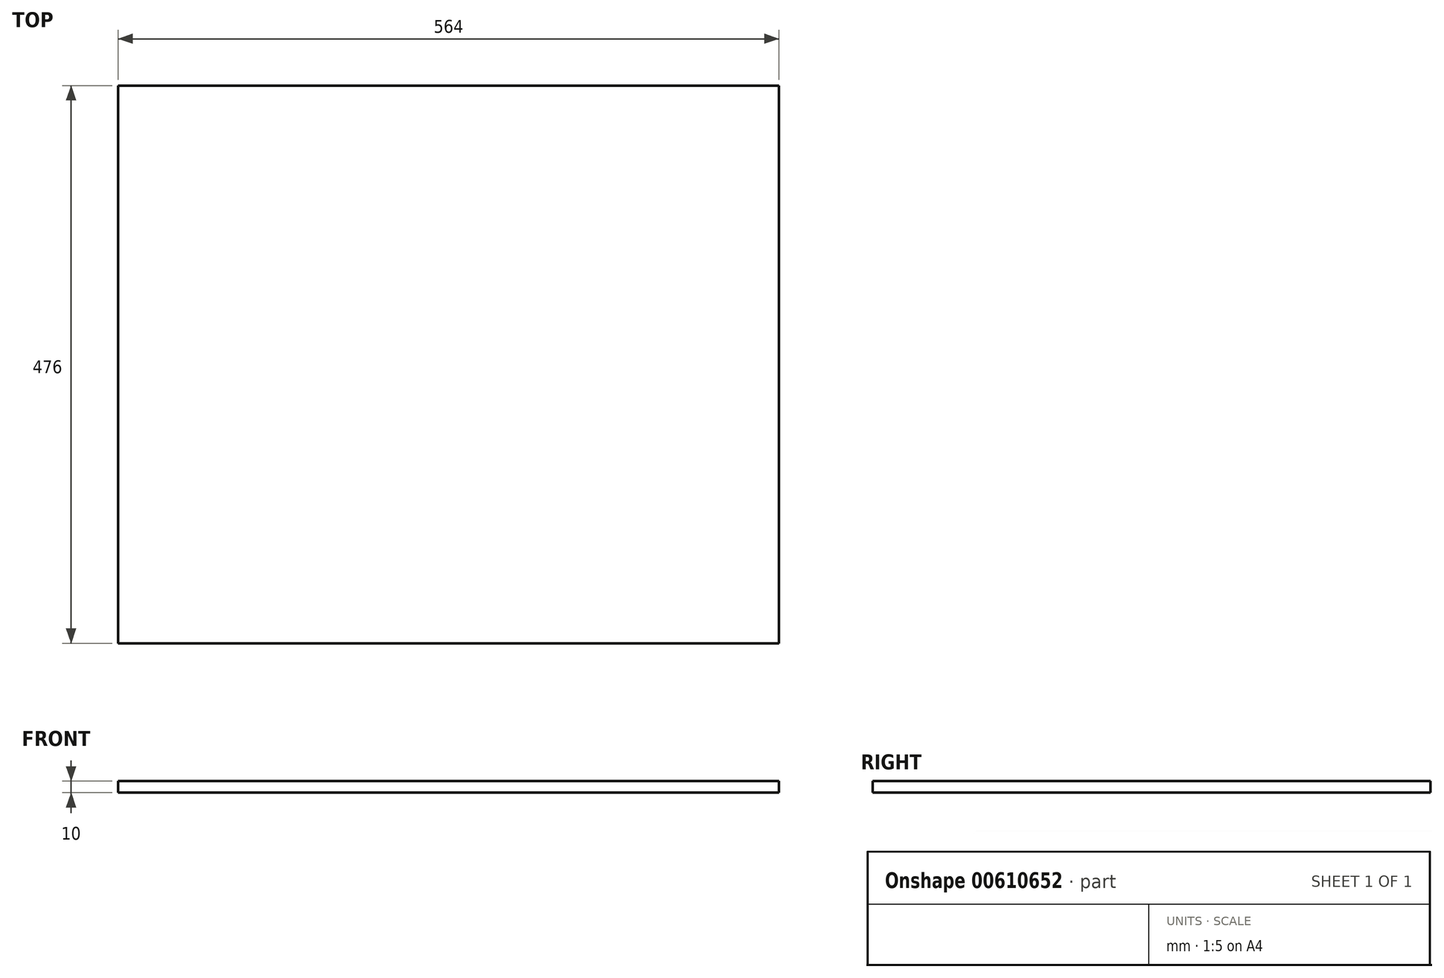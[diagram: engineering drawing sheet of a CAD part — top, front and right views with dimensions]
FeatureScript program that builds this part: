
annotation { "Feature Type Name" : "Feature", "Feature Type Description" : "" }
export const myFeature = defineFeature(function(context is Context, id is Id, definition is map)
    precondition{}
    {
        {
            var Q0;
            Q0=qCreatedBy(makeId("Top.planeOp"),FACE);
            var sketch = newSketch(context, id + "F0", { "sketchPlane" : qUnion([Q0])});
            skLineSegment(sketch, "E0.bottom", {"start": v(-336.36, 152.6) * mm, "end": v(227.64, 152.6) * mm});
            skLineSegment(sketch, "E0.top", {"start": v(-336.36, -323.4) * mm, "end": v(227.64, -323.4) * mm});
            skLineSegment(sketch, "E0.left", {"start": v(-336.36, 152.6) * mm, "end": v(-336.36, -323.4) * mm});
            skLineSegment(sketch, "E0.right", {"start": v(227.64, 152.6) * mm, "end": v(227.64, -323.4) * mm});
            skSolve(sketch);
        }
        {
            var Q0;
            Q0=makeQuery(id+"F0.imprint","IMPRINT",FACE,{"disambiguationData":[TD([[makeQuery(id+"F0.imprint","IMPRINT",EDGE,{"derivedFrom":sQuery(id+"F0.wireOp",EDGE,"E0.bottom")}),-1.0]])]});
            extrude(context, id + "F1", {"entities" : qUnion([Q0]), "depth" : 10 * mm, "offsetDistance" : 25 * mm});
        }
    });
